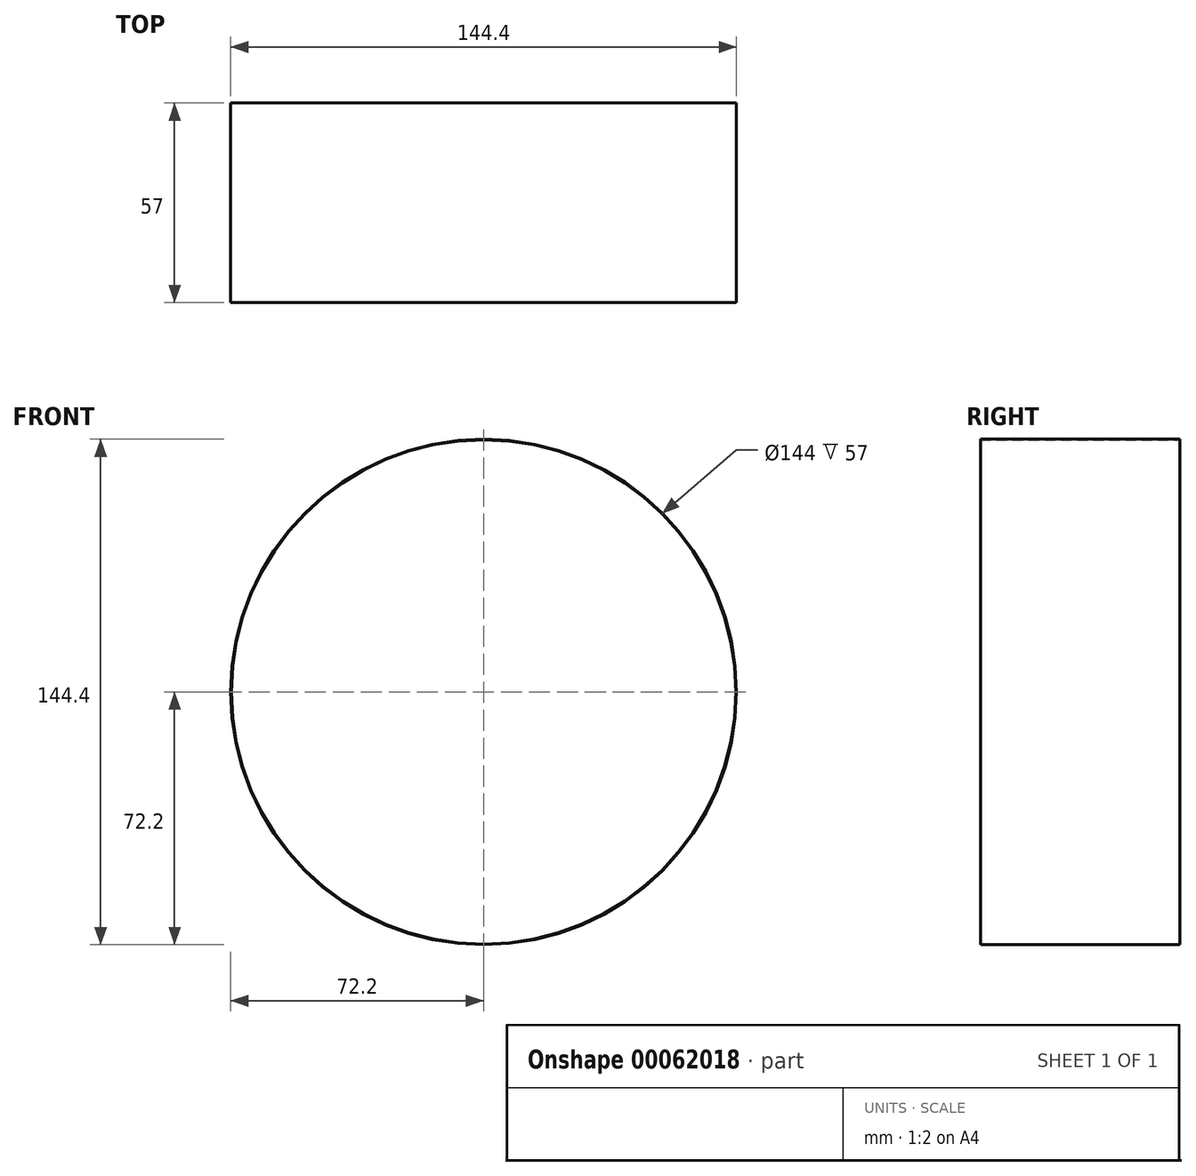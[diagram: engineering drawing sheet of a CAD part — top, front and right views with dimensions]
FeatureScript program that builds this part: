
annotation { "Feature Type Name" : "Feature", "Feature Type Description" : "" }
export const myFeature = defineFeature(function(context is Context, id is Id, definition is map)
    precondition{}
    {
        {
            var Q0;
            Q0=qCreatedBy(makeId("Front.planeOp"),FACE);
            var sketch = newSketch(context, id + "F0", { "sketchPlane" : qUnion([Q0])});
            skCircle(sketch, "E0", {"center": v(0, 0) * mm, "radius": 72 * mm});
            skCircle(sketch, "E1.0", {"center": v(0, 0) * mm, "radius": 72.2 * mm});
            skSolve(sketch);
        }
        {
            var Q0;
            Q0=makeQuery(id+"F0.imprint","IMPRINT",FACE,{"disambiguationData":[TD([[makeQuery(id+"F0.imprint","IMPRINT",EDGE,{"derivedFrom":sQuery(id+"F0.wireOp",EDGE,"E0")}),-1.0]])]});
            extrude(context, id + "F1", {"entities" : qUnion([Q0]), "depth" : 57 * mm});
        }
    });
